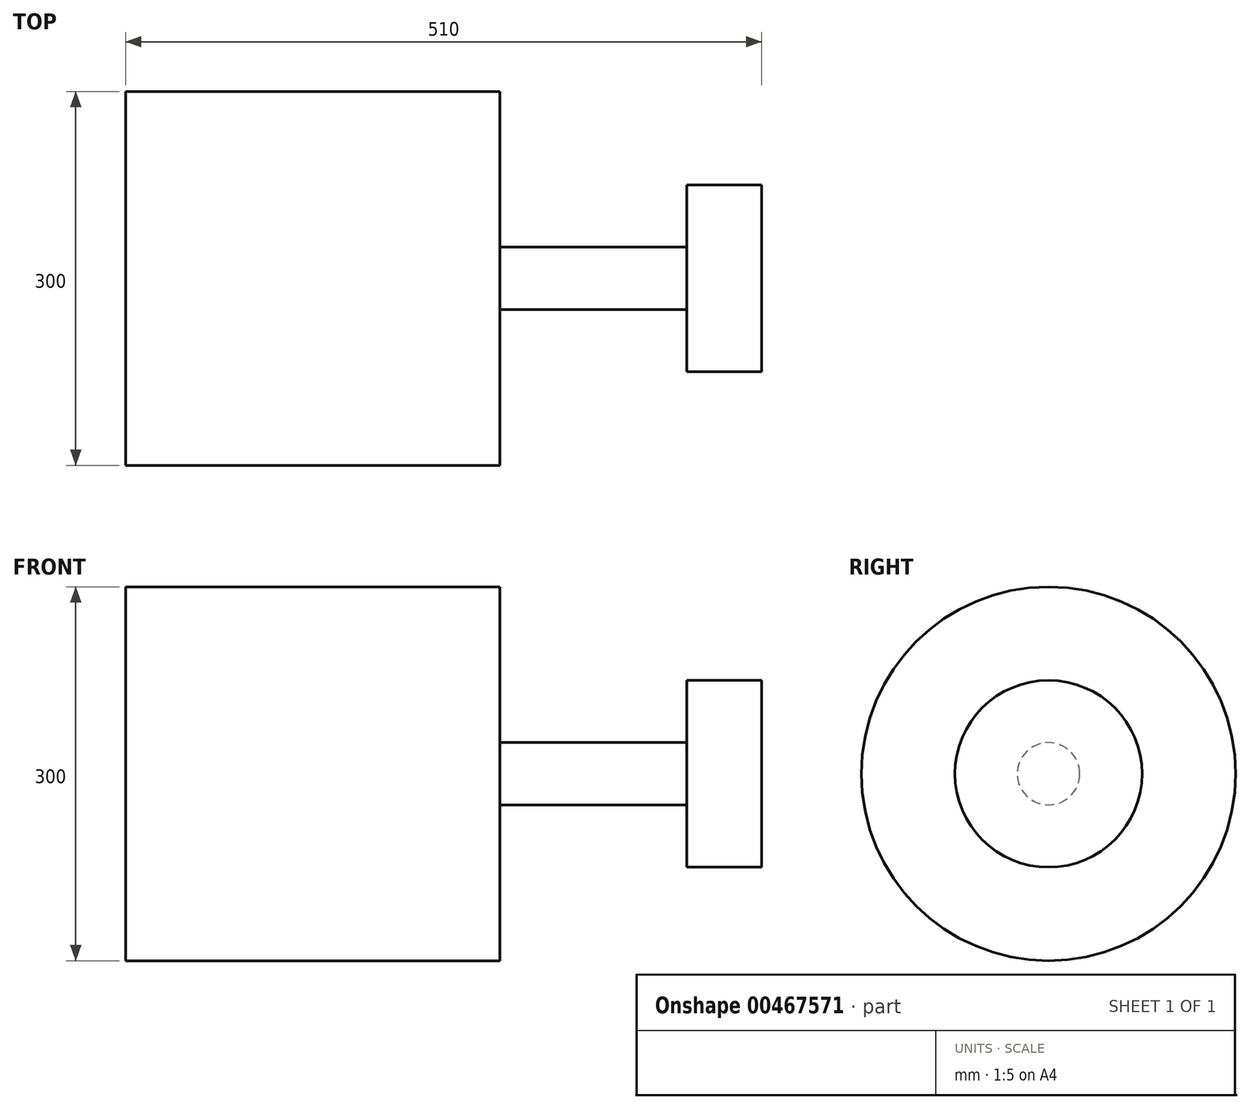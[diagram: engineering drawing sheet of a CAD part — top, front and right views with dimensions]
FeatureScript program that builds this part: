
annotation { "Feature Type Name" : "Feature", "Feature Type Description" : "" }
export const myFeature = defineFeature(function(context is Context, id is Id, definition is map)
    precondition{}
    {
        {
            var Q0;
            Q0=qCreatedBy(makeId("Front.planeOp"),FACE);
            var sketch = newSketch(context, id + "F0", { "sketchPlane" : qUnion([Q0])});
            skLineSegment(sketch, "E0", {"start": v(0, 0) * mm, "end": v(0, 150) * mm});
            skLineSegment(sketch, "E1", {"start": v(0, 150) * mm, "end": v(300, 150) * mm});
            skLineSegment(sketch, "E2", {"start": v(300, 150) * mm, "end": v(300, 25) * mm});
            skLineSegment(sketch, "E3", {"start": v(300, 25) * mm, "end": v(450, 25) * mm});
            skLineSegment(sketch, "E4", {"start": v(450, 25) * mm, "end": v(450, 75) * mm});
            skLineSegment(sketch, "E5", {"start": v(450, 75) * mm, "end": v(510, 75) * mm});
            skLineSegment(sketch, "E6", {"start": v(510, 75) * mm, "end": v(510, 0) * mm});
            skLineSegment(sketch, "E7", {"start": v(510, 0) * mm, "end": v(0, 0) * mm});
            skSolve(sketch);
        }
        {
            var Q0;
            Q0=makeQuery(id+"F0.imprint","IMPRINT",FACE,{"disambiguationData":[TD([[makeQuery(id+"F0.imprint","IMPRINT",EDGE,{"derivedFrom":sQuery(id+"F0.wireOp",EDGE,"E0")}),-1.0]])]});
            var Q1;
            Q1=sQuery(id+"F0.wireOp",EDGE,"E7");
            revolve(context, id + "F1", {"entities" : qUnion([Q0]), "axis" : qUnion([Q1]), "revolveType" : RevolveType.FULL});
        }
    });
